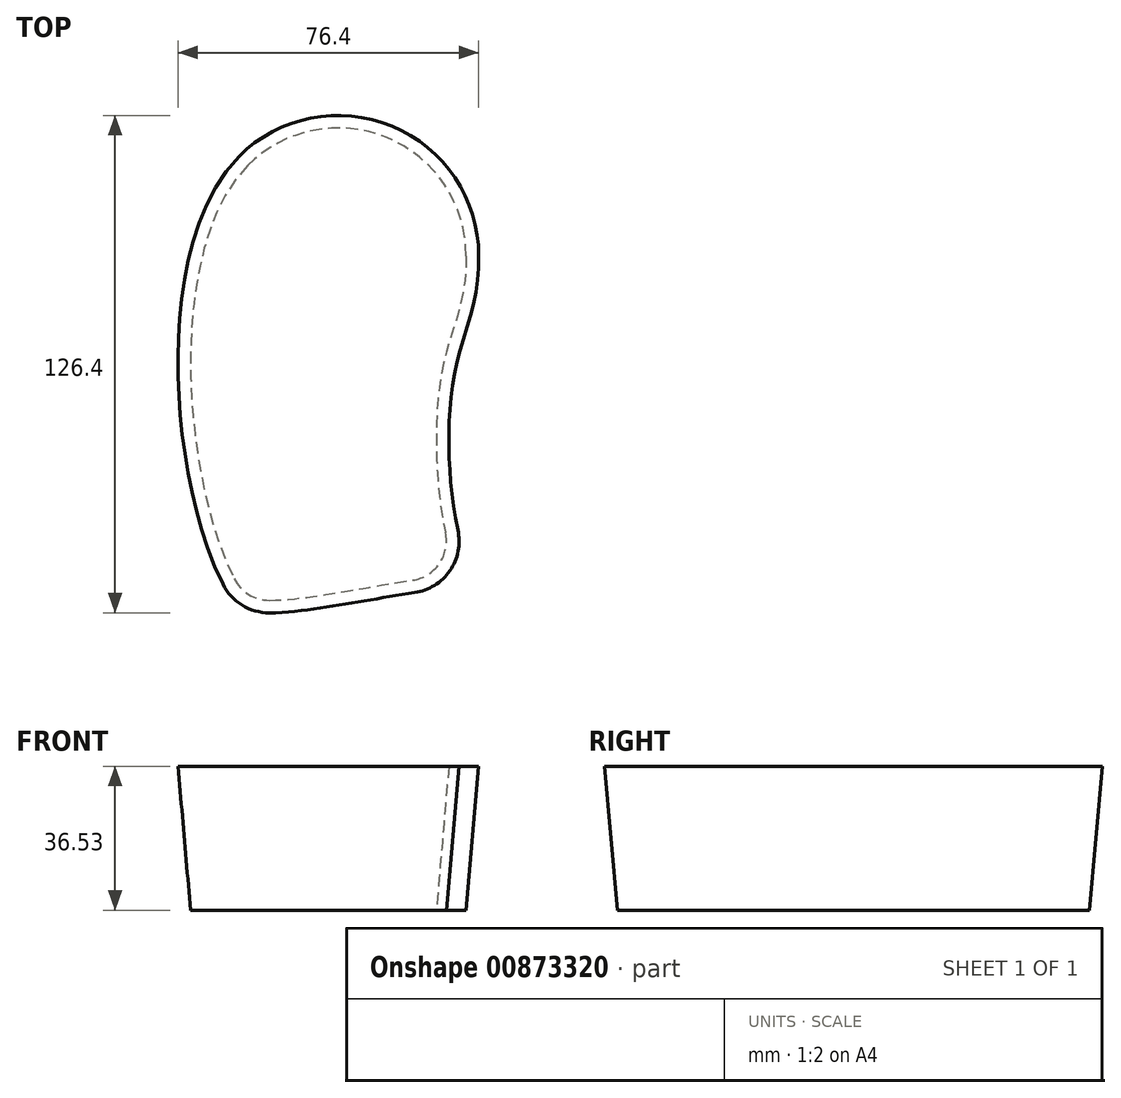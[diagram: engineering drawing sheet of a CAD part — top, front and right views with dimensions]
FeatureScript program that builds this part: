
annotation { "Feature Type Name" : "Feature", "Feature Type Description" : "" }
export const myFeature = defineFeature(function(context is Context, id is Id, definition is map)
    precondition{}
    {
        {
            var Q0;
            Q0=qCreatedBy(makeId("Top.planeOp"),FACE);
            var sketch = newSketch(context, id + "F0", { "sketchPlane" : qUnion([Q0])});
            skArc(sketch, "E0", {"start": v(32.5, 0) * mm, "mid": v(12.44, 30.03) * mm, "end": v(-22.98, 22.98) * mm});
            skFitSpline(sketch, "E1", {"points": [v(-22.98, 22.98) * mm, v(-24.83, -84.99) * mm], "startDerivative": vector(-63.64, -63.64) * mm, "endDerivative": vector(45, -77.94) * mm});
            skFitSpline(sketch, "E2", {"points": [v(-24.83, -84.99) * mm, v(38.24, -86.12) * mm], "startDerivative": vector(8.62, -29.47) * mm, "endDerivative": vector(-19.5, -43.47) * mm});
            skArc(sketch, "E3.filletArc", {"start": v(-26.45, -81.96) * mm, "mid": v(-22.76, -86) * mm, "end": v(-17.5, -87.5) * mm});
            skFitSpline(sketch, "E4", {"points": [v(32.5, 0) * mm, v(25.5, -35) * mm, v(38.24, -86.12) * mm], "startDerivative": vector(0, -99.67) * mm, "endDerivative": vector(63, 6.92) * mm});
            skLineSegment(sketch, "E5", {"start": v(0, 0) * mm, "end": v(-22.98, 22.98) * mm, "construction": true});
            skLineSegment(sketch, "E6", {"start": v(-37.5, 32.5) * mm, "end": v(-37.5, -87.5) * mm, "construction": true});
            skLineSegment(sketch, "E7", {"start": v(-37.5, -87.5) * mm, "end": v(32.5, -87.5) * mm, "construction": true});
            skLineSegment(sketch, "E8", {"start": v(32.5, -87.5) * mm, "end": v(32.5, 32.5) * mm, "construction": true});
            skLineSegment(sketch, "E9", {"start": v(32.5, 32.5) * mm, "end": v(-37.5, 32.5) * mm, "construction": true});
            skArc(sketch, "E10.filletArc", {"start": v(18.96, -82.4) * mm, "mid": v(25.73, -78.17) * mm, "end": v(27.26, -70.34) * mm});
            skLineSegment(sketch, "E11", {"start": v(0, 32.5) * mm, "end": v(0, 0) * mm, "construction": true});
            skLineSegment(sketch, "E12", {"start": v(-22.98, 22.98) * mm, "end": v(-44.2, 1.77) * mm, "construction": true});
            skLineSegment(sketch, "E13", {"start": v(-37.5, -77.5) * mm, "end": v(-17.5, -77.5) * mm, "construction": true});
            skLineSegment(sketch, "E14", {"start": v(-17.5, -77.5) * mm, "end": v(-17.5, -87.5) * mm, "construction": true});
            skLineSegment(sketch, "E15", {"start": v(-17.5, -87.5) * mm, "end": v(-17.5, -77.5) * mm, "construction": true});
            skLineSegment(sketch, "E16", {"start": v(-24.83, -84.99) * mm, "end": v(-39.83, -59) * mm, "construction": true});
            skLineSegment(sketch, "E17", {"start": v(32.5, -72.5) * mm, "end": v(17.5, -72.5) * mm, "construction": true});
            skLineSegment(sketch, "E18", {"start": v(17.5, -87.5) * mm, "end": v(17.5, -72.5) * mm, "construction": true});
            skLineSegment(sketch, "E19", {"start": v(25.5, -35) * mm, "end": v(32.5, -35) * mm, "construction": true});
            skSolve(sketch);
        }
        {
            var Q0;
            Q0=makeQuery(id+"F0.imprint","IMPRINT",FACE,{"disambiguationData":[TD([[makeQuery(id+"F0.imprint","IMPRINT",EDGE,{"derivedFrom":sQuery(id+"F0.wireOp",EDGE,"E0")}),1.0]])]});
            extrude(context, id + "F1", {"entities" : qUnion([Q0]), "depth" : 36.53 * mm, "offsetDistance" : 25 * mm, "hasDraft" : true, "draftAngle" : 5 * degree});
        }
        {
            var Q0;
            Q0=qCreatedBy(makeId("Front.planeOp"),FACE);
            cPlane(context, id + "F2", {"entities" : qUnion([Q0]), "cplaneType" : CPlaneType.OFFSET, "offset" : 98.32 * mm, "width" : 150 * mm, "height" : 150 * mm});
        }
    });
